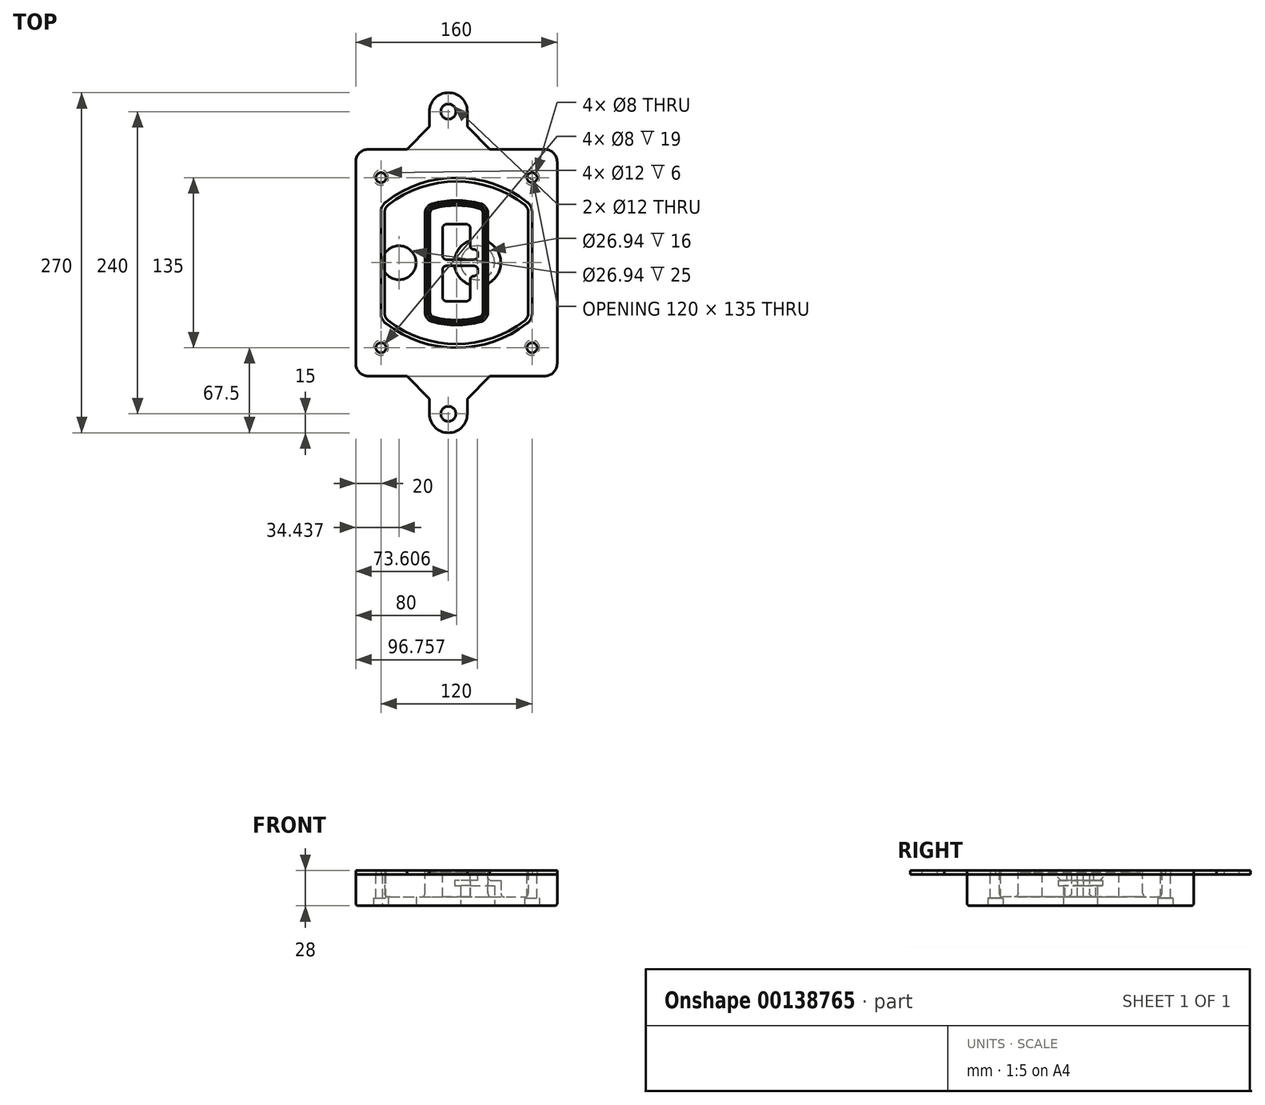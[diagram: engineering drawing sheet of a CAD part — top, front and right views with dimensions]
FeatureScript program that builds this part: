
annotation { "Feature Type Name" : "Feature", "Feature Type Description" : "" }
export const myFeature = defineFeature(function(context is Context, id is Id, definition is map)
    precondition{}
    {
        {
            var Q0;
            Q0=qCreatedBy(makeId("Top.planeOp"),FACE);
            var sketch = newSketch(context, id + "F0", { "sketchPlane" : qUnion([Q0])});
            skPoint(sketch, "E0.rect.middle", {"position": v(0, 0) * mm});
            skLineSegment(sketch, "E1.bottom", {"start": v(-70, -90) * mm, "end": v(70, -90) * mm});
            skLineSegment(sketch, "E1.top", {"start": v(-70, 90) * mm, "end": v(70, 90) * mm});
            skLineSegment(sketch, "E1.left", {"start": v(-80, -80) * mm, "end": v(-80, 80) * mm});
            skLineSegment(sketch, "E1.right", {"start": v(80, -80) * mm, "end": v(80, 80) * mm});
            skLineSegment(sketch, "E2", {"start": v(-80, 90) * mm, "end": v(80, -90) * mm, "construction": true});
            skLineSegment(sketch, "E3", {"start": v(80, 90) * mm, "end": v(-80, -90) * mm, "construction": true});
            skCircle(sketch, "E4", {"center": v(-60, 67.5) * mm, "radius": 4 * mm});
            skCircle(sketch, "E5", {"center": v(60, 67.5) * mm, "radius": 4 * mm});
            skCircle(sketch, "E6", {"center": v(60, -67.5) * mm, "radius": 4 * mm});
            skCircle(sketch, "E7", {"center": v(-60, -67.5) * mm, "radius": 4 * mm});
            skLineSegment(sketch, "E8", {"start": v(-60, 67.5) * mm, "end": v(60, 67.5) * mm, "construction": true});
            skLineSegment(sketch, "E9", {"start": v(60, 67.5) * mm, "end": v(60, -67.5) * mm, "construction": true});
            skLineSegment(sketch, "E10", {"start": v(60, -67.5) * mm, "end": v(-60, -67.5) * mm, "construction": true});
            skLineSegment(sketch, "E11", {"start": v(-60, -67.5) * mm, "end": v(-60, 67.5) * mm, "construction": true});
            skLineSegment(sketch, "E12", {"start": v(-60, 40.3) * mm, "end": v(-60, -40.3) * mm});
            skLineSegment(sketch, "E13", {"start": v(60, 40.3) * mm, "end": v(60, -40.3) * mm});
            skArc(sketch, "E14", {"start": v(56.15, 48.18) * mm, "mid": v(0, 67.5) * mm, "end": v(-56.15, 48.18) * mm});
            skArc(sketch, "E15", {"start": v(-56.15, -48.18) * mm, "mid": v(0, -67.5) * mm, "end": v(56.15, -48.18) * mm});
            skLineSegment(sketch, "E16", {"start": v(-60, 0) * mm, "end": v(60, 0) * mm, "construction": true});
            skPoint(sketch, "E17.visualSharp", {"position": v(-60, -45) * mm});
            skArc(sketch, "E17.filletArc", {"start": v(-60, -40.3) * mm, "mid": v(-58.99, -44.68) * mm, "end": v(-56.15, -48.18) * mm});
            skPoint(sketch, "E18.visualSharp", {"position": v(-60, 45) * mm});
            skArc(sketch, "E18.filletArc", {"start": v(-56.15, 48.18) * mm, "mid": v(-58.99, 44.68) * mm, "end": v(-60, 40.3) * mm});
            skPoint(sketch, "E19.visualSharp", {"position": v(60, 45) * mm});
            skArc(sketch, "E19.filletArc", {"start": v(60, 40.3) * mm, "mid": v(58.99, 44.68) * mm, "end": v(56.15, 48.18) * mm});
            skPoint(sketch, "E20.visualSharp", {"position": v(60, -45) * mm});
            skArc(sketch, "E20.filletArc", {"start": v(56.15, -48.18) * mm, "mid": v(58.99, -44.68) * mm, "end": v(60, -40.3) * mm});
            skPoint(sketch, "E21.visualSharp", {"position": v(-80, 90) * mm});
            skArc(sketch, "E21.filletArc", {"start": v(-70, 90) * mm, "mid": v(-77.07, 87.07) * mm, "end": v(-80, 80) * mm});
            skPoint(sketch, "E22.visualSharp", {"position": v(80, 90) * mm});
            skArc(sketch, "E22.filletArc", {"start": v(80, 80) * mm, "mid": v(77.07, 87.07) * mm, "end": v(70, 90) * mm});
            skPoint(sketch, "E23.visualSharp", {"position": v(80, -90) * mm});
            skArc(sketch, "E23.filletArc", {"start": v(70, -90) * mm, "mid": v(77.07, -87.07) * mm, "end": v(80, -80) * mm});
            skPoint(sketch, "E24.visualSharp", {"position": v(-80, -90) * mm});
            skArc(sketch, "E24.filletArc", {"start": v(-80, -80) * mm, "mid": v(-77.07, -87.07) * mm, "end": v(-70, -90) * mm});
            skArc(sketch, "E25.0", {"start": v(57, 40.3) * mm, "mid": v(56.3, 43.36) * mm, "end": v(54.3, 45.81) * mm});
            skLineSegment(sketch, "E25.1", {"start": v(57, 40.3) * mm, "end": v(57, -40.3) * mm});
            skArc(sketch, "E25.2", {"start": v(54.3, -45.81) * mm, "mid": v(56.3, -43.36) * mm, "end": v(57, -40.3) * mm});
            skArc(sketch, "E25.3", {"start": v(-54.3, -45.81) * mm, "mid": v(0, -64.5) * mm, "end": v(54.3, -45.81) * mm});
            skArc(sketch, "E25.4", {"start": v(-57, -40.3) * mm, "mid": v(-56.3, -43.36) * mm, "end": v(-54.3, -45.81) * mm});
            skArc(sketch, "E25.5", {"start": v(54.3, 45.81) * mm, "mid": v(0, 64.5) * mm, "end": v(-54.3, 45.81) * mm});
            skLineSegment(sketch, "E25.6", {"start": v(-57, 40.3) * mm, "end": v(-57, -40.3) * mm});
            skArc(sketch, "E25.7", {"start": v(-54.3, 45.81) * mm, "mid": v(-56.3, 43.36) * mm, "end": v(-57, 40.3) * mm});
            skArc(sketch, "E26.0", {"start": v(-58.62, 51.33) * mm, "mid": v(-62.58, 46.43) * mm, "end": v(-64, 40.3) * mm});
            skArc(sketch, "E26.1", {"start": v(58.62, 51.33) * mm, "mid": v(0, 71.5) * mm, "end": v(-58.62, 51.33) * mm});
            skArc(sketch, "E26.2", {"start": v(64, 40.3) * mm, "mid": v(62.58, 46.43) * mm, "end": v(58.62, 51.33) * mm});
            skLineSegment(sketch, "E26.3", {"start": v(64, 40.3) * mm, "end": v(64, -40.3) * mm});
            skArc(sketch, "E26.4", {"start": v(58.62, -51.33) * mm, "mid": v(62.58, -46.43) * mm, "end": v(64, -40.3) * mm});
            skLineSegment(sketch, "E26.5", {"start": v(-64, 40.3) * mm, "end": v(-64, -40.3) * mm});
            skArc(sketch, "E26.6", {"start": v(-58.62, -51.33) * mm, "mid": v(0, -71.5) * mm, "end": v(58.62, -51.33) * mm});
            skArc(sketch, "E26.7", {"start": v(-64, -40.3) * mm, "mid": v(-62.58, -46.43) * mm, "end": v(-58.62, -51.33) * mm});
            skSolve(sketch);
        }
        {
            var Q0;
            Q0=makeQuery(id+"F0.imprint","IMPRINT",FACE,{"disambiguationData":[TD([[makeQuery(id+"F0.imprint","IMPRINT",EDGE,{"derivedFrom":sQuery(id+"F0.wireOp",EDGE,"E1.bottom")}),1.0]])]});
            var Q1;
            Q1=makeQuery(id+"F0.imprint","IMPRINT",FACE,{"disambiguationData":[TD([[makeQuery(id+"F0.imprint","IMPRINT",EDGE,{"derivedFrom":sQuery(id+"F0.wireOp",EDGE,"E12")}),1.0]])]});
            var Q2;
            Q2=makeQuery(id+"F0.imprint","IMPRINT",FACE,{"disambiguationData":[TD([[makeQuery(id+"F0.imprint","IMPRINT",EDGE,{"derivedFrom":sQuery(id+"F0.wireOp",EDGE,"E25.0")}),1.0]])]});
            var Q3;
            Q3=makeQuery(id+"F0.imprint","IMPRINT",FACE,{"disambiguationData":[TD([[makeQuery(id+"F0.imprint","IMPRINT",EDGE,{"derivedFrom":sQuery(id+"F0.wireOp",EDGE,"E12")}),-1.0]])]});
            extrude(context, id + "F1", {"entities" : qUnion([Q0, Q1, Q2, Q3]), "oppositeDirection" : true, "depth" : 25 * mm});
        }
        {
            var Q0;
            Q0=makeQuery(id+"F0.imprint","IMPRINT",FACE,{"disambiguationData":[TD([[makeQuery(id+"F0.imprint","IMPRINT",EDGE,{"derivedFrom":sQuery(id+"F0.wireOp",EDGE,"E12")}),1.0]])]});
            extrude(context, id + "F2", {"entities" : qUnion([Q0]), "operationType" : NewBodyOperationType.ADD, "depth" : 3 * mm});
        }
        {
            var Q0;
            Q0=makeQuery(id+"F0.imprint","IMPRINT",FACE,{"disambiguationData":[TD([[makeQuery(id+"F0.imprint","IMPRINT",EDGE,{"derivedFrom":sQuery(id+"F0.wireOp",EDGE,"E25.0")}),1.0]])]});
            extrude(context, id + "F3", {"entities" : qUnion([Q0]), "operationType" : NewBodyOperationType.REMOVE, "oppositeDirection" : true, "depth" : 18 * mm});
        }
        {
            var Q0;
            Q0=makeQuery(id+"F2.opExtrude","CAP_FACE",FACE,{"disambiguationData":[OSD([sQuery(id+"F0.wireOp",EDGE,"E12"),sQuery(id+"F0.wireOp",EDGE,"E13"),sQuery(id+"F0.wireOp",EDGE,"E14"),sQuery(id+"F0.wireOp",EDGE,"E15"),sQuery(id+"F0.wireOp",EDGE,"E17.filletArc"),sQuery(id+"F0.wireOp",EDGE,"E18.filletArc"),sQuery(id+"F0.wireOp",EDGE,"E19.filletArc"),sQuery(id+"F0.wireOp",EDGE,"E20.filletArc"),sQuery(id+"F0.wireOp",EDGE,"E25.0"),sQuery(id+"F0.wireOp",EDGE,"E25.1"),sQuery(id+"F0.wireOp",EDGE,"E25.2"),sQuery(id+"F0.wireOp",EDGE,"E25.3"),sQuery(id+"F0.wireOp",EDGE,"E25.4"),sQuery(id+"F0.wireOp",EDGE,"E25.5"),sQuery(id+"F0.wireOp",EDGE,"E25.6"),sQuery(id+"F0.wireOp",EDGE,"E25.7")])],"isStart":false});
            var sketch = newSketch(context, id + "F4", { "sketchPlane" : qUnion([Q0])});
            skArc(sketch, "E27.0", {"start": v(-19.08, -46.97) * mm, "mid": v(0, -49.5) * mm, "end": v(19.08, -46.97) * mm});
            skArc(sketch, "E28.0", {"start": v(19.08, 46.97) * mm, "mid": v(0, 49.5) * mm, "end": v(-19.08, 46.97) * mm});
            skLineSegment(sketch, "E29", {"start": v(-25, 39.25) * mm, "end": v(-25, -39.25) * mm});
            skLineSegment(sketch, "E30", {"start": v(25, 39.25) * mm, "end": v(25, -39.25) * mm});
            skLineSegment(sketch, "E31", {"start": v(-25, 45.1) * mm, "end": v(25, 45.1) * mm, "construction": true});
            skLineSegment(sketch, "E32", {"start": v(-25, -45.1) * mm, "end": v(25, -45.1) * mm, "construction": true});
            skPoint(sketch, "E33.visualSharp", {"position": v(-25, 45.1) * mm});
            skArc(sketch, "E33.filletArc", {"start": v(-19.08, 46.97) * mm, "mid": v(-23.35, 44.11) * mm, "end": v(-25, 39.25) * mm});
            skPoint(sketch, "E34.visualSharp", {"position": v(25, 45.1) * mm});
            skArc(sketch, "E34.filletArc", {"start": v(25, 39.25) * mm, "mid": v(23.35, 44.11) * mm, "end": v(19.08, 46.97) * mm});
            skPoint(sketch, "E35.visualSharp", {"position": v(25, -45.1) * mm});
            skArc(sketch, "E35.filletArc", {"start": v(19.08, -46.97) * mm, "mid": v(23.35, -44.11) * mm, "end": v(25, -39.25) * mm});
            skPoint(sketch, "E36.visualSharp", {"position": v(-25, -45.1) * mm});
            skArc(sketch, "E36.filletArc", {"start": v(-25, -39.25) * mm, "mid": v(-23.35, -44.11) * mm, "end": v(-19.08, -46.97) * mm});
            skArc(sketch, "E37.0", {"start": v(54.3, 45.81) * mm, "mid": v(0, 64.5) * mm, "end": v(-54.3, 45.81) * mm});
            skArc(sketch, "E37.1", {"start": v(-54.3, 45.81) * mm, "mid": v(-56.3, 43.36) * mm, "end": v(-57, 40.3) * mm});
            skLineSegment(sketch, "E37.2", {"start": v(-57, 40.3) * mm, "end": v(-57, -40.3) * mm});
            skArc(sketch, "E37.3", {"start": v(-57, -40.3) * mm, "mid": v(-56.3, -43.36) * mm, "end": v(-54.3, -45.81) * mm});
            skArc(sketch, "E37.4", {"start": v(-54.3, -45.81) * mm, "mid": v(0, -64.5) * mm, "end": v(54.3, -45.81) * mm});
            skArc(sketch, "E37.5", {"start": v(54.3, -45.81) * mm, "mid": v(56.3, -43.36) * mm, "end": v(57, -40.3) * mm});
            skLineSegment(sketch, "E37.6", {"start": v(57, 40.3) * mm, "end": v(57, -40.3) * mm});
            skArc(sketch, "E37.7", {"start": v(57, 40.3) * mm, "mid": v(56.3, 43.36) * mm, "end": v(54.3, 45.81) * mm});
            skLineSegment(sketch, "E38.0", {"start": v(23, 39.25) * mm, "end": v(23, -39.25) * mm});
            skArc(sketch, "E38.1", {"start": v(18.56, -45.04) * mm, "mid": v(21.76, -42.9) * mm, "end": v(23, -39.25) * mm});
            skArc(sketch, "E38.2", {"start": v(-18.56, -45.04) * mm, "mid": v(0, -47.5) * mm, "end": v(18.56, -45.04) * mm});
            skArc(sketch, "E38.3", {"start": v(-23, -39.25) * mm, "mid": v(-21.76, -42.9) * mm, "end": v(-18.56, -45.04) * mm});
            skLineSegment(sketch, "E38.4", {"start": v(-23, 39.25) * mm, "end": v(-23, -39.25) * mm});
            skArc(sketch, "E38.5", {"start": v(23, 39.25) * mm, "mid": v(21.76, 42.9) * mm, "end": v(18.56, 45.04) * mm});
            skArc(sketch, "E38.6", {"start": v(-18.56, 45.04) * mm, "mid": v(-21.76, 42.9) * mm, "end": v(-23, 39.25) * mm});
            skArc(sketch, "E38.7", {"start": v(18.56, 45.04) * mm, "mid": v(0, 47.5) * mm, "end": v(-18.56, 45.04) * mm});
            skArc(sketch, "E39.0", {"start": v(21, 39.25) * mm, "mid": v(20.18, 41.68) * mm, "end": v(18.04, 43.1) * mm});
            skLineSegment(sketch, "E39.1", {"start": v(21, 39.25) * mm, "end": v(21, -39.25) * mm});
            skArc(sketch, "E39.2", {"start": v(18.04, -43.1) * mm, "mid": v(20.18, -41.68) * mm, "end": v(21, -39.25) * mm});
            skArc(sketch, "E39.3", {"start": v(-18.04, -43.1) * mm, "mid": v(0, -45.5) * mm, "end": v(18.04, -43.1) * mm});
            skArc(sketch, "E39.4", {"start": v(-21, -39.25) * mm, "mid": v(-20.18, -41.68) * mm, "end": v(-18.04, -43.1) * mm});
            skArc(sketch, "E39.5", {"start": v(18.04, 43.1) * mm, "mid": v(0, 45.5) * mm, "end": v(-18.04, 43.1) * mm});
            skLineSegment(sketch, "E39.6", {"start": v(-21, 39.25) * mm, "end": v(-21, -39.25) * mm});
            skArc(sketch, "E39.7", {"start": v(-18.04, 43.1) * mm, "mid": v(-20.18, 41.68) * mm, "end": v(-21, 39.25) * mm});
            skLineSegment(sketch, "E40", {"start": v(-25, 0) * mm, "end": v(25, 0) * mm, "construction": true});
            skLineSegment(sketch, "E41", {"start": v(-11, 5.5) * mm, "end": v(-11, 27.5) * mm});
            skLineSegment(sketch, "E42", {"start": v(-8, 30.5) * mm, "end": v(8, 30.5) * mm});
            skLineSegment(sketch, "E43", {"start": v(11, 27.5) * mm, "end": v(11, 13.5) * mm});
            skLineSegment(sketch, "E44", {"start": v(14, 10.5) * mm, "end": v(14, 10.5) * mm});
            skLineSegment(sketch, "E45", {"start": v(17, 7.5) * mm, "end": v(17, 5.5) * mm});
            skLineSegment(sketch, "E46", {"start": v(14, 2.5) * mm, "end": v(-8, 2.5) * mm});
            skPoint(sketch, "E47.visualSharp", {"position": v(-11, 30.5) * mm});
            skArc(sketch, "E47.filletArc", {"start": v(-8, 30.5) * mm, "mid": v(-10.12, 29.62) * mm, "end": v(-11, 27.5) * mm});
            skPoint(sketch, "E48.visualSharp", {"position": v(11, 30.5) * mm});
            skArc(sketch, "E48.filletArc", {"start": v(11, 27.5) * mm, "mid": v(10.12, 29.62) * mm, "end": v(8, 30.5) * mm});
            skPoint(sketch, "E49.visualSharp", {"position": v(11, 10.5) * mm});
            skArc(sketch, "E49.filletArc", {"start": v(11, 13.5) * mm, "mid": v(11.88, 11.38) * mm, "end": v(14, 10.5) * mm});
            skPoint(sketch, "E50.visualSharp", {"position": v(17, 10.5) * mm});
            skArc(sketch, "E50.filletArc", {"start": v(17, 7.5) * mm, "mid": v(16.12, 9.62) * mm, "end": v(14, 10.5) * mm});
            skPoint(sketch, "E51.visualSharp", {"position": v(17, 2.5) * mm});
            skArc(sketch, "E51.filletArc", {"start": v(14, 2.5) * mm, "mid": v(16.12, 3.38) * mm, "end": v(17, 5.5) * mm});
            skPoint(sketch, "E52.visualSharp", {"position": v(-11, 2.5) * mm});
            skArc(sketch, "E52.filletArc", {"start": v(-11, 5.5) * mm, "mid": v(-10.12, 3.38) * mm, "end": v(-8, 2.5) * mm});
            skLineSegment(sketch, "E53.0.MirrorCS", {"start": v(14, -2.5) * mm, "end": v(-8, -2.5) * mm});
            skArc(sketch, "E54.0.MirrorCS", {"start": v(-11, -5.5) * mm, "mid": v(-10.12, -3.38) * mm, "end": v(-8, -2.5) * mm});
            skLineSegment(sketch, "E55.0.MirrorCS", {"start": v(-11, -5.5) * mm, "end": v(-11, -27.5) * mm});
            skArc(sketch, "E56.0.MirrorCS", {"start": v(-8, -30.5) * mm, "mid": v(-10.12, -29.62) * mm, "end": v(-11, -27.5) * mm});
            skLineSegment(sketch, "E57.0.MirrorCS", {"start": v(-8, -30.5) * mm, "end": v(8, -30.5) * mm});
            skArc(sketch, "E58.0.MirrorCS", {"start": v(11, -27.5) * mm, "mid": v(10.12, -29.62) * mm, "end": v(8, -30.5) * mm});
            skLineSegment(sketch, "E59.0.MirrorCS", {"start": v(11, -27.5) * mm, "end": v(11, -13.5) * mm});
            skArc(sketch, "E60.0.MirrorCS", {"start": v(11, -13.5) * mm, "mid": v(11.88, -11.38) * mm, "end": v(14, -10.5) * mm});
            skArc(sketch, "E61.0.MirrorCS", {"start": v(17, -7.5) * mm, "mid": v(16.12, -9.62) * mm, "end": v(14, -10.5) * mm});
            skLineSegment(sketch, "E62.0.MirrorCS", {"start": v(17, -7.5) * mm, "end": v(17, -5.5) * mm});
            skArc(sketch, "E63.0.MirrorCS", {"start": v(14, -2.5) * mm, "mid": v(16.12, -3.38) * mm, "end": v(17, -5.5) * mm});
            skSolve(sketch);
        }
        {
            var Q0;
            Q0=makeQuery(id+"F4.imprint","IMPRINT",FACE,{"disambiguationData":[TD([[makeQuery(id+"F4.imprint","IMPRINT",EDGE,{"derivedFrom":sQuery(id+"F4.wireOp",EDGE,"E27.0")}),1.0]])]});
            var Q1;
            Q1=makeQuery(id+"F4.imprint","IMPRINT",FACE,{"disambiguationData":[TD([[makeQuery(id+"F4.imprint","IMPRINT",EDGE,{"derivedFrom":sQuery(id+"F4.wireOp",EDGE,"E38.0")}),-1.0]])]});
            var Q2;
            Q2=makeQuery(id+"F4.imprint","IMPRINT",FACE,{"disambiguationData":[TD([[makeQuery(id+"F4.imprint","IMPRINT",EDGE,{"derivedFrom":sQuery(id+"F4.wireOp",EDGE,"E39.0")}),1.0]])]});
            extrude(context, id + "F5", {"entities" : qUnion([Q0, Q1, Q2]), "operationType" : NewBodyOperationType.ADD, "endBound" : BoundingType.UP_TO_NEXT, "oppositeDirection" : true, "depth" : 25 * mm});
        }
        {
            var Q0;
            Q0=makeQuery(id+"F4.imprint","IMPRINT",FACE,{"disambiguationData":[TD([[makeQuery(id+"F4.imprint","IMPRINT",EDGE,{"derivedFrom":sQuery(id+"F4.wireOp",EDGE,"E38.0")}),-1.0]])]});
            extrude(context, id + "F6", {"entities" : qUnion([Q0]), "operationType" : NewBodyOperationType.REMOVE, "oppositeDirection" : true, "depth" : 2 * mm});
        }
        {
            var Q0;
            Q0=makeQuery(id+"F1.opExtrude","CAP_FACE",FACE,{"disambiguationData":[OSD([sQuery(id+"F0.wireOp",EDGE,"E1.bottom"),sQuery(id+"F0.wireOp",EDGE,"E1.top"),sQuery(id+"F0.wireOp",EDGE,"E1.left"),sQuery(id+"F0.wireOp",EDGE,"E1.right"),sQuery(id+"F0.wireOp",EDGE,"E4"),sQuery(id+"F0.wireOp",EDGE,"E5"),sQuery(id+"F0.wireOp",EDGE,"E6"),sQuery(id+"F0.wireOp",EDGE,"E7"),sQuery(id+"F0.wireOp",EDGE,"E21.filletArc"),sQuery(id+"F0.wireOp",EDGE,"E22.filletArc"),sQuery(id+"F0.wireOp",EDGE,"E23.filletArc"),sQuery(id+"F0.wireOp",EDGE,"E24.filletArc")])],"isStart":false});
            var sketch = newSketch(context, id + "F7", { "sketchPlane" : qUnion([Q0])});
            skCircle(sketch, "E64", {"center": v(16.76, 0) * mm, "radius": 13.47 * mm});
            skCircle(sketch, "E65", {"center": v(-45.56, 0) * mm, "radius": 13.47 * mm});
            skLineSegment(sketch, "E66", {"start": v(80, 0) * mm, "end": v(-80, 0) * mm});
            skCircle(sketch, "E67", {"center": v(16.76, 0) * mm, "radius": 18.47 * mm});
            skCircle(sketch, "E68", {"center": v(60, -67.5) * mm, "radius": 6 * mm});
            skCircle(sketch, "E69", {"center": v(-60, -67.5) * mm, "radius": 6 * mm});
            skCircle(sketch, "E70", {"center": v(-60, 67.5) * mm, "radius": 6 * mm});
            skCircle(sketch, "E71", {"center": v(60, 67.5) * mm, "radius": 6 * mm});
            skSolve(sketch);
        }
        {
            var Q0;
            {var subQ1=sQuery(id+"F7.wireOp",EDGE,"E66");var subQ4=sQuery(id+"F7.wireOp",EDGE,"E64");var subQ6=makeQuery(id+"F7.imprint","INTERSECT",VERTEX,{"disambiguationData":[OD(0.0)],"derivedFrom":[subQ4,subQ1]});Q0=makeQuery(id+"F7.imprint","IMPRINT",FACE,{"disambiguationData":[TD([[makeQuery(id+"F7.imprint","IMPRINT",EDGE,{"disambiguationData":[TD([[subQ6,-1.0]])],"derivedFrom":subQ4}),-1.0]])]});}
            var Q1;
            {var subQ0=sQuery(id+"F7.wireOp",EDGE,"E66");var subQ1=sQuery(id+"F7.wireOp",EDGE,"E64");var subQ3=makeQuery(id+"F7.imprint","INTERSECT",VERTEX,{"disambiguationData":[OD(0.0)],"derivedFrom":[subQ1,subQ0]});Q1=makeQuery(id+"F7.imprint","IMPRINT",FACE,{"disambiguationData":[TD([[makeQuery(id+"F7.imprint","IMPRINT",EDGE,{"disambiguationData":[TD([[subQ3,-1.0]])],"derivedFrom":subQ1}),1.0]])]});}
            var Q2;
            {var subQ0=sQuery(id+"F7.wireOp",EDGE,"E66");var subQ1=sQuery(id+"F7.wireOp",EDGE,"E64");var subQ3=makeQuery(id+"F7.imprint","INTERSECT",VERTEX,{"disambiguationData":[OD(0.0)],"derivedFrom":[subQ1,subQ0]});Q2=makeQuery(id+"F7.imprint","IMPRINT",FACE,{"disambiguationData":[TD([[makeQuery(id+"F7.imprint","IMPRINT",EDGE,{"disambiguationData":[TD([[subQ3,1.0]])],"derivedFrom":subQ1}),1.0]])]});}
            var Q3;
            {var subQ1=sQuery(id+"F7.wireOp",EDGE,"E66");var subQ4=sQuery(id+"F7.wireOp",EDGE,"E64");var subQ6=makeQuery(id+"F7.imprint","INTERSECT",VERTEX,{"disambiguationData":[OD(0.0)],"derivedFrom":[subQ4,subQ1]});Q3=makeQuery(id+"F7.imprint","IMPRINT",FACE,{"disambiguationData":[TD([[makeQuery(id+"F7.imprint","IMPRINT",EDGE,{"disambiguationData":[TD([[subQ6,1.0]])],"derivedFrom":subQ4}),-1.0]])]});}
            extrude(context, id + "F8", {"entities" : qUnion([Q0, Q1, Q2, Q3]), "operationType" : NewBodyOperationType.ADD, "oppositeDirection" : true, "depth" : 20 * mm});
        }
        {
            var Q0;
            {var subQ0=sQuery(id+"F7.wireOp",EDGE,"E66");var subQ1=sQuery(id+"F7.wireOp",EDGE,"E64");var subQ3=makeQuery(id+"F7.imprint","INTERSECT",VERTEX,{"disambiguationData":[OD(0.0)],"derivedFrom":[subQ1,subQ0]});Q0=makeQuery(id+"F7.imprint","IMPRINT",FACE,{"disambiguationData":[TD([[makeQuery(id+"F7.imprint","IMPRINT",EDGE,{"disambiguationData":[TD([[subQ3,-1.0]])],"derivedFrom":subQ1}),1.0]])]});}
            var Q1;
            {var subQ0=sQuery(id+"F7.wireOp",EDGE,"E66");var subQ1=sQuery(id+"F7.wireOp",EDGE,"E64");var subQ3=makeQuery(id+"F7.imprint","INTERSECT",VERTEX,{"disambiguationData":[OD(0.0)],"derivedFrom":[subQ1,subQ0]});Q1=makeQuery(id+"F7.imprint","IMPRINT",FACE,{"disambiguationData":[TD([[makeQuery(id+"F7.imprint","IMPRINT",EDGE,{"disambiguationData":[TD([[subQ3,1.0]])],"derivedFrom":subQ1}),1.0]])]});}
            extrude(context, id + "F9", {"entities" : qUnion([Q0, Q1]), "operationType" : NewBodyOperationType.REMOVE, "oppositeDirection" : true, "depth" : 16 * mm});
        }
        {
            var Q0;
            {var subQ0=sQuery(id+"F7.wireOp",EDGE,"E66");var subQ1=sQuery(id+"F7.wireOp",EDGE,"E65");var subQ3=makeQuery(id+"F7.imprint","INTERSECT",VERTEX,{"disambiguationData":[OD(0.0)],"derivedFrom":[subQ1,subQ0]});Q0=makeQuery(id+"F7.imprint","IMPRINT",FACE,{"disambiguationData":[TD([[makeQuery(id+"F7.imprint","IMPRINT",EDGE,{"disambiguationData":[TD([[subQ3,-1.0]])],"derivedFrom":subQ1}),1.0]])]});}
            var Q1;
            {var subQ0=sQuery(id+"F7.wireOp",EDGE,"E66");var subQ1=sQuery(id+"F7.wireOp",EDGE,"E65");var subQ3=makeQuery(id+"F7.imprint","INTERSECT",VERTEX,{"disambiguationData":[OD(0.0)],"derivedFrom":[subQ1,subQ0]});Q1=makeQuery(id+"F7.imprint","IMPRINT",FACE,{"disambiguationData":[TD([[makeQuery(id+"F7.imprint","IMPRINT",EDGE,{"disambiguationData":[TD([[subQ3,1.0]])],"derivedFrom":subQ1}),1.0]])]});}
            extrude(context, id + "F10", {"entities" : qUnion([Q0, Q1]), "operationType" : NewBodyOperationType.REMOVE, "oppositeDirection" : true, "depth" : 25 * mm});
        }
        {
            var Q0;
            Q0=makeQuery(id+"F7.imprint","IMPRINT",FACE,{"disambiguationData":[TD([[makeQuery(id+"F7.imprint","IMPRINT",EDGE,{"derivedFrom":sQuery(id+"F7.wireOp",EDGE,"E68")}),1.0]])]});
            var Q1;
            Q1=makeQuery(id+"F7.imprint","IMPRINT",FACE,{"disambiguationData":[TD([[makeQuery(id+"F7.imprint","IMPRINT",EDGE,{"derivedFrom":makeQuery(id+"F1.opExtrude","CAP_EDGE",EDGE,{"disambiguationData":[OSD([sQuery(id+"F0.wireOp",EDGE,"E5")])],"isStart":false})}),-1.0]])]});
            var Q2;
            Q2=makeQuery(id+"F7.imprint","IMPRINT",FACE,{"disambiguationData":[TD([[makeQuery(id+"F7.imprint","IMPRINT",EDGE,{"derivedFrom":sQuery(id+"F7.wireOp",EDGE,"E69")}),1.0]])]});
            var Q3;
            Q3=makeQuery(id+"F7.imprint","IMPRINT",FACE,{"disambiguationData":[TD([[makeQuery(id+"F7.imprint","IMPRINT",EDGE,{"derivedFrom":makeQuery(id+"F1.opExtrude","CAP_EDGE",EDGE,{"disambiguationData":[OSD([sQuery(id+"F0.wireOp",EDGE,"E4")])],"isStart":false})}),-1.0]])]});
            var Q4;
            Q4=makeQuery(id+"F7.imprint","IMPRINT",FACE,{"disambiguationData":[TD([[makeQuery(id+"F7.imprint","IMPRINT",EDGE,{"derivedFrom":sQuery(id+"F7.wireOp",EDGE,"E70")}),1.0]])]});
            var Q5;
            Q5=makeQuery(id+"F7.imprint","IMPRINT",FACE,{"disambiguationData":[TD([[makeQuery(id+"F7.imprint","IMPRINT",EDGE,{"derivedFrom":makeQuery(id+"F1.opExtrude","CAP_EDGE",EDGE,{"disambiguationData":[OSD([sQuery(id+"F0.wireOp",EDGE,"E7")])],"isStart":false})}),-1.0]])]});
            var Q6;
            Q6=makeQuery(id+"F7.imprint","IMPRINT",FACE,{"disambiguationData":[TD([[makeQuery(id+"F7.imprint","IMPRINT",EDGE,{"derivedFrom":sQuery(id+"F7.wireOp",EDGE,"E71")}),1.0]])]});
            var Q7;
            Q7=makeQuery(id+"F7.imprint","IMPRINT",FACE,{"disambiguationData":[TD([[makeQuery(id+"F7.imprint","IMPRINT",EDGE,{"derivedFrom":makeQuery(id+"F1.opExtrude","CAP_EDGE",EDGE,{"disambiguationData":[OSD([sQuery(id+"F0.wireOp",EDGE,"E6")])],"isStart":false})}),-1.0]])]});
            extrude(context, id + "F11", {"entities" : qUnion([Q0, Q1, Q2, Q3, Q4, Q5, Q6, Q7]), "operationType" : NewBodyOperationType.REMOVE, "oppositeDirection" : true, "depth" : 6 * mm});
        }
        {
            var Q0;
            Q0=makeQuery(id+"F9.boolean.opBoolean","COPY",FACE,{"derivedFrom":makeQuery(id+"F9.opExtrude","CAP_FACE",FACE,{"disambiguationData":[OSD([sQuery(id+"F7.wireOp",EDGE,"E64")])],"isStart":false})});
            var sketch = newSketch(context, id + "F12", { "sketchPlane" : qUnion([Q0])});
            skArc(sketch, "E72.0", {"start": v(11, 17.55) * mm, "mid": v(2.57, 11.82) * mm, "end": v(-1.54, 2.5) * mm});
            skArc(sketch, "E72.1", {"start": v(-1.54, -2.5) * mm, "mid": v(2.57, -11.82) * mm, "end": v(11, -17.55) * mm});
            skLineSegment(sketch, "E73", {"start": v(-1.54, -2.5) * mm, "end": v(14, -2.5) * mm});
            skLineSegment(sketch, "E74.0", {"start": v(14, 2.5) * mm, "end": v(-1.54, 2.5) * mm});
            skArc(sketch, "E74.1", {"start": v(14, 2.5) * mm, "mid": v(16.12, 3.38) * mm, "end": v(17, 5.5) * mm});
            skLineSegment(sketch, "E74.2", {"start": v(17, 7.5) * mm, "end": v(17, 5.5) * mm});
            skArc(sketch, "E74.3", {"start": v(17, 7.5) * mm, "mid": v(16.12, 9.62) * mm, "end": v(14, 10.5) * mm});
            skArc(sketch, "E74.4", {"start": v(11, 13.5) * mm, "mid": v(11.88, 11.38) * mm, "end": v(14, 10.5) * mm});
            skLineSegment(sketch, "E74.5", {"start": v(11, 17.55) * mm, "end": v(11, 13.5) * mm});
            skLineSegment(sketch, "E74.7", {"start": v(14, -2.5) * mm, "end": v(-1.54, -2.5) * mm});
            skArc(sketch, "E74.8", {"start": v(14, -2.5) * mm, "mid": v(16.12, -3.38) * mm, "end": v(17, -5.5) * mm});
            skLineSegment(sketch, "E74.9", {"start": v(17, -7.5) * mm, "end": v(17, -5.5) * mm});
            skArc(sketch, "E74.10", {"start": v(17, -7.5) * mm, "mid": v(16.12, -9.62) * mm, "end": v(14, -10.5) * mm});
            skArc(sketch, "E74.11", {"start": v(11, -13.5) * mm, "mid": v(11.88, -11.38) * mm, "end": v(14, -10.5) * mm});
            skLineSegment(sketch, "E74.12", {"start": v(11, -17.55) * mm, "end": v(11, -13.5) * mm});
            skPoint(sketch, "E75.orphan", {"position": v(11, -27.5) * mm});
            skPoint(sketch, "E76.orphan", {"position": v(-8, -2.5) * mm});
            skPoint(sketch, "E77.orphan", {"position": v(-8, 2.5) * mm});
            skPoint(sketch, "E78.orphan", {"position": v(11, 27.5) * mm});
            skSolve(sketch);
        }
        {
            var Q0;
            {var subQ7=sQuery(id+"F12.wireOp",EDGE,"E72.0");var subQ14=sQuery(id+"F12.wireOp",EDGE,"E72.1");var subQ16=sQuery(id+"F12.wireOp",EDGE,"E74.1");var subQ18=sQuery(id+"F12.wireOp",EDGE,"E74.8");Q0=qUnion([makeQuery(id+"F12.imprint","IMPRINT",FACE,{"disambiguationData":[TD([[makeQuery(id+"F12.imprint","IMPRINT",EDGE,{"derivedFrom":subQ7}),1.0]])]}),makeQuery(id+"F12.imprint","IMPRINT",FACE,{"disambiguationData":[TD([[makeQuery(id+"F12.imprint","IMPRINT",EDGE,{"derivedFrom":subQ14}),1.0]])]}),makeQuery(id+"F12.imprint","IMPRINT",FACE,{"disambiguationData":[TD([[makeQuery(id+"F12.imprint","IMPRINT",EDGE,{"derivedFrom":subQ16}),1.0]])]}),makeQuery(id+"F12.imprint","IMPRINT",FACE,{"disambiguationData":[TD([[makeQuery(id+"F12.imprint","IMPRINT",EDGE,{"derivedFrom":subQ18}),-1.0]])]})]);}
            var Q1;
            Q1=makeQuery(id+"F5.boolean.opBoolean","SPLIT",FACE,{"disambiguationData":[TD([makeQuery(id+"F5.opExtrude","SWEPT_FACE",FACE,{"disambiguationData":[OSD([sQuery(id+"F4.wireOp",EDGE,"E41")])]})])],"derivedFrom":makeQuery(id+"F3.boolean.opBoolean","COPY",FACE,{"derivedFrom":makeQuery(id+"F3.opExtrude","CAP_FACE",FACE,{"disambiguationData":[OSD([sQuery(id+"F0.wireOp",EDGE,"E25.0"),sQuery(id+"F0.wireOp",EDGE,"E25.1"),sQuery(id+"F0.wireOp",EDGE,"E25.2"),sQuery(id+"F0.wireOp",EDGE,"E25.3"),sQuery(id+"F0.wireOp",EDGE,"E25.4"),sQuery(id+"F0.wireOp",EDGE,"E25.5"),sQuery(id+"F0.wireOp",EDGE,"E25.6"),sQuery(id+"F0.wireOp",EDGE,"E25.7")])],"isStart":false})})});
            extrude(context, id + "F13", {"entities" : qUnion([Q0]), "operationType" : NewBodyOperationType.REMOVE, "endBound" : BoundingType.UP_TO_SURFACE, "endBoundEntityFace" : qUnion([Q1]), "depth" : 25 * mm});
        }
        {
            var Q0;
            Q0=makeQuery(id+"F3.boolean.opBoolean","COPY",EDGE,{"derivedFrom":makeQuery(id+"F3.opExtrude","CAP_EDGE",EDGE,{"disambiguationData":[OSD([sQuery(id+"F0.wireOp",EDGE,"E25.6")])],"isStart":false})});
            var Q1;
            Q1=makeQuery(id+"F8.boolean.opBoolean","INTERSECT",EDGE,{"derivedFrom":[makeQuery(id+"F5.opExtrude","SWEPT_FACE",FACE,{"disambiguationData":[OSD([sQuery(id+"F4.wireOp",EDGE,"E30")])]}),makeQuery(id+"F8.opExtrude","CAP_FACE",FACE,{"disambiguationData":[OSD([sQuery(id+"F7.wireOp",EDGE,"E67")])],"isStart":false})]});
            var Q2;
            Q2=makeQuery(id+"F8.boolean.opBoolean","INTERSECT",EDGE,{"disambiguationData":[OD(1.0)],"derivedFrom":[makeQuery(id+"F5.opExtrude","SWEPT_FACE",FACE,{"disambiguationData":[OSD([sQuery(id+"F4.wireOp",EDGE,"E30")])]}),makeQuery(id+"F8.opExtrude","SWEPT_FACE",FACE,{"disambiguationData":[OSD([sQuery(id+"F7.wireOp",EDGE,"E67")])]})]});
            var Q3;
            {var subQ0=sQuery(id+"F4.wireOp",EDGE,"E30");Q3=makeQuery(id+"F8.boolean.opBoolean","SPLIT",EDGE,{"disambiguationData":[TD([makeQuery(id+"F5.opExtrude","SWEPT_FACE",FACE,{"disambiguationData":[OSD([sQuery(id+"F4.wireOp",EDGE,"E35.filletArc")])]})])],"derivedFrom":makeQuery(id+"F5.opExtrude","CAP_EDGE",EDGE,{"disambiguationData":[OSD([subQ0])],"isStart":false})});}
            var Q4;
            {var subQ0=sQuery(id+"F0.wireOp",EDGE,"E25.7");var subQ1=sQuery(id+"F0.wireOp",EDGE,"E25.1");var subQ2=sQuery(id+"F0.wireOp",EDGE,"E25.6");var subQ3=sQuery(id+"F0.wireOp",EDGE,"E25.5");var subQ4=sQuery(id+"F0.wireOp",EDGE,"E25.4");var subQ5=sQuery(id+"F0.wireOp",EDGE,"E25.0");var subQ6=sQuery(id+"F0.wireOp",EDGE,"E25.2");var subQ7=sQuery(id+"F0.wireOp",EDGE,"E25.3");Q4=makeQuery(id+"F8.boolean.opBoolean","INTERSECT",EDGE,{"derivedFrom":[makeQuery(id+"F5.boolean.opBoolean","SPLIT",FACE,{"disambiguationData":[TD([makeQuery(id+"F2.opExtrude","SWEPT_FACE",FACE,{"disambiguationData":[OSD([subQ5])]})])],"derivedFrom":makeQuery(id+"F3.boolean.opBoolean","COPY",FACE,{"derivedFrom":makeQuery(id+"F3.opExtrude","CAP_FACE",FACE,{"disambiguationData":[OSD([subQ5,subQ1,subQ6,subQ7,subQ4,subQ3,subQ2,subQ0])],"isStart":false})})}),makeQuery(id+"F8.opExtrude","SWEPT_FACE",FACE,{"disambiguationData":[OSD([sQuery(id+"F7.wireOp",EDGE,"E67")])]})]});}
            var Q5;
            Q5=makeQuery(id+"F8.boolean.opBoolean","INTERSECT",EDGE,{"disambiguationData":[OD(0.0)],"derivedFrom":[makeQuery(id+"F5.opExtrude","SWEPT_FACE",FACE,{"disambiguationData":[OSD([sQuery(id+"F4.wireOp",EDGE,"E30")])]}),makeQuery(id+"F8.opExtrude","SWEPT_FACE",FACE,{"disambiguationData":[OSD([sQuery(id+"F7.wireOp",EDGE,"E67")])]})]});
            fillet(context, id + "F14", {"entities" : qUnion([Q0, Q1, Q2, Q3, Q4, Q5]), "radius" : 3 * mm, "tangentPropagation" : true, "allowEdgeOverflow" : false});
        }
        {
            var Q0;
            Q0=makeQuery(id+"F1.opExtrude","CAP_EDGE",EDGE,{"disambiguationData":[OSD([sQuery(id+"F0.wireOp",EDGE,"E1.bottom")])],"isStart":false});
            fillet(context, id + "F15", {"entities" : qUnion([Q0]), "radius" : 2 * mm, "tangentPropagation" : true, "allowEdgeOverflow" : false});
        }
        {
            var Q0;
            {var subQ0=sQuery(id+"F0.wireOp",EDGE,"E22.filletArc");var subQ1=sQuery(id+"F0.wireOp",EDGE,"E7");var subQ2=sQuery(id+"F0.wireOp",EDGE,"E6");var subQ3=sQuery(id+"F0.wireOp",EDGE,"E5");var subQ4=sQuery(id+"F0.wireOp",EDGE,"E4");var subQ5=sQuery(id+"F0.wireOp",EDGE,"E1.bottom");var subQ6=sQuery(id+"F0.wireOp",EDGE,"E21.filletArc");var subQ7=sQuery(id+"F0.wireOp",EDGE,"E1.top");var subQ8=sQuery(id+"F0.wireOp",EDGE,"E1.left");var subQ9=sQuery(id+"F0.wireOp",EDGE,"E1.right");var subQ10=sQuery(id+"F0.wireOp",EDGE,"E23.filletArc");var subQ11=sQuery(id+"F0.wireOp",EDGE,"E24.filletArc");Q0=makeQuery(id+"F2.boolean.opBoolean","SPLIT",FACE,{"disambiguationData":[TD([makeQuery(id+"F1.opExtrude","SWEPT_FACE",FACE,{"disambiguationData":[OSD([subQ5])]})])],"derivedFrom":makeQuery(id+"F1.opExtrude","CAP_FACE",FACE,{"disambiguationData":[OSD([subQ5,subQ7,subQ8,subQ9,subQ4,subQ3,subQ2,subQ1,subQ6,subQ0,subQ10,subQ11])],"isStart":true})});}
            var sketch = newSketch(context, id + "F16", { "sketchPlane" : qUnion([Q0])});
            skLineSegment(sketch, "E79", {"start": v(-39.4, 90) * mm, "end": v(-21.4, 108) * mm});
            skLineSegment(sketch, "E80", {"start": v(-21.4, 120) * mm, "end": v(-21.4, 108) * mm});
            skLineSegment(sketch, "E81", {"start": v(26.6, 90) * mm, "end": v(8.6, 108) * mm});
            skLineSegment(sketch, "E82", {"start": v(8.6, 108) * mm, "end": v(8.6, 120) * mm});
            skCircle(sketch, "E83", {"center": v(-6.4, 120) * mm, "radius": 6 * mm});
            skArc(sketch, "E84", {"start": v(8.6, 120) * mm, "mid": v(-6.4, 135) * mm, "end": v(-21.4, 120) * mm});
            skLineSegment(sketch, "E85", {"start": v(-6.4, 120) * mm, "end": v(-6.4, 90) * mm, "construction": true});
            skPoint(sketch, "E85.endSnap0", {"position": v(0, 90) * mm});
            skLineSegment(sketch, "E86", {"start": v(-80, 0) * mm, "end": v(80, 0) * mm, "construction": true});
            skPoint(sketch, "E87.MirrorP", {"position": v(0, -90) * mm});
            skLineSegment(sketch, "E88.MirrorCS", {"start": v(-39.4, -90) * mm, "end": v(-21.4, -108) * mm});
            skLineSegment(sketch, "E89.MirrorCS", {"start": v(-21.4, -120) * mm, "end": v(-21.4, -108) * mm});
            skLineSegment(sketch, "E90.MirrorCS", {"start": v(26.6, -90) * mm, "end": v(8.6, -108) * mm});
            skLineSegment(sketch, "E91.MirrorCS", {"start": v(8.6, -108) * mm, "end": v(8.6, -120) * mm});
            skCircle(sketch, "E92.MirrorC", {"center": v(-6.4, -120) * mm, "radius": 6 * mm});
            skArc(sketch, "E93.MirrorCS", {"start": v(8.6, -120) * mm, "mid": v(-6.4, -135) * mm, "end": v(-21.4, -120) * mm});
            skLineSegment(sketch, "E94.MirrorCS", {"start": v(-6.4, -120) * mm, "end": v(-6.4, -90) * mm, "construction": true});
            skSolve(sketch);
        }
        {
            var Q0;
            {var subQ1=sQuery(id+"F16.wireOp",EDGE,"E88.MirrorCS");Q0=makeQuery(id+"F16.imprint","IMPRINT",FACE,{"disambiguationData":[TD([[makeQuery(id+"F16.imprint","IMPRINT",EDGE,{"derivedFrom":subQ1}),1.0]])]});}
            var Q1;
            {var subQ1=sQuery(id+"F16.wireOp",EDGE,"E79");Q1=makeQuery(id+"F16.imprint","IMPRINT",FACE,{"disambiguationData":[TD([[makeQuery(id+"F16.imprint","IMPRINT",EDGE,{"derivedFrom":subQ1}),-1.0]])]});}
            var Q2;
            Q2=makeQuery(id+"F16.imprint","IMPRINT",FACE,{"disambiguationData":[TD([[makeQuery(id+"F16.imprint","IMPRINT",EDGE,{"derivedFrom":makeQuery(id+"F1.opExtrude","CAP_EDGE",EDGE,{"disambiguationData":[OSD([sQuery(id+"F0.wireOp",EDGE,"E1.left")])],"isStart":true})}),-1.0]])]});
            var Q3;
            Q3=makeQuery(id+"F2.opExtrude","CAP_FACE",FACE,{"disambiguationData":[OSD([sQuery(id+"F0.wireOp",EDGE,"E12"),sQuery(id+"F0.wireOp",EDGE,"E13"),sQuery(id+"F0.wireOp",EDGE,"E14"),sQuery(id+"F0.wireOp",EDGE,"E15"),sQuery(id+"F0.wireOp",EDGE,"E17.filletArc"),sQuery(id+"F0.wireOp",EDGE,"E18.filletArc"),sQuery(id+"F0.wireOp",EDGE,"E19.filletArc"),sQuery(id+"F0.wireOp",EDGE,"E20.filletArc"),sQuery(id+"F0.wireOp",EDGE,"E25.0"),sQuery(id+"F0.wireOp",EDGE,"E25.1"),sQuery(id+"F0.wireOp",EDGE,"E25.2"),sQuery(id+"F0.wireOp",EDGE,"E25.3"),sQuery(id+"F0.wireOp",EDGE,"E25.4"),sQuery(id+"F0.wireOp",EDGE,"E25.5"),sQuery(id+"F0.wireOp",EDGE,"E25.6"),sQuery(id+"F0.wireOp",EDGE,"E25.7")])],"isStart":false});
            extrude(context, id + "F17", {"entities" : qUnion([Q0, Q1, Q2]), "endBound" : BoundingType.UP_TO_SURFACE, "endBoundEntityFace" : qUnion([Q3]), "depth" : 25 * mm});
        }
    });
